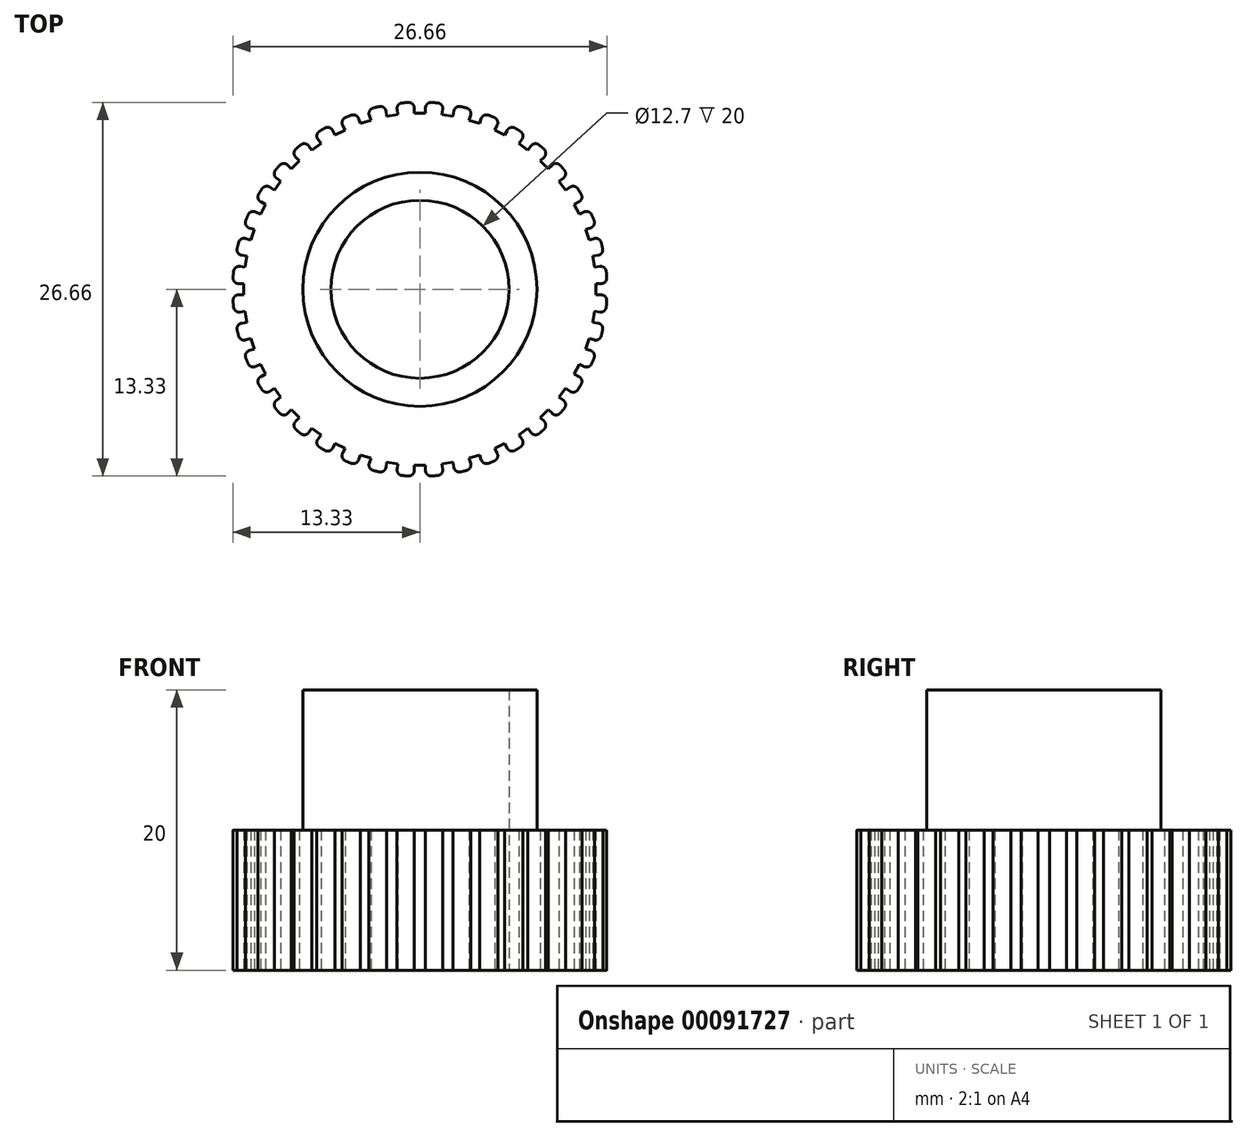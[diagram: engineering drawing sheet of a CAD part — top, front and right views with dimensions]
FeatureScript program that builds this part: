
annotation { "Feature Type Name" : "Feature", "Feature Type Description" : "" }
export const myFeature = defineFeature(function(context is Context, id is Id, definition is map)
    precondition{}
    {
        {
            var Q0;
            Q0=qCreatedBy(makeId("Top.planeOp"),FACE);
            var sketch = newSketch(context, id + "F0", { "sketchPlane" : qUnion([Q0])});
            skCircle(sketch, "E0", {"center": v(0, 0) * mm, "radius": 6.35 * mm});
            skCircle(sketch, "E1", {"center": v(0, 0) * mm, "radius": 8.35 * mm});
            skCircle(sketch, "E2", {"center": v(0, 0) * mm, "radius": 13.35 * mm});
            skLineSegment(sketch, "E3", {"start": v(0, 0) * mm, "end": v(0, 13.35) * mm, "construction": true});
            skLineSegment(sketch, "E4", {"start": v(-0.4, 12.93) * mm, "end": v(-0.4, 12.55) * mm});
            skLineSegment(sketch, "E5", {"start": v(-0.4, 12.55) * mm, "end": v(0.4, 12.55) * mm});
            skLineSegment(sketch, "E6", {"start": v(0.4, 12.55) * mm, "end": v(0.4, 12.93) * mm});
            skArc(sketch, "E7", {"start": v(-0.4, 12.93) * mm, "mid": v(-0.53, 13.22) * mm, "end": v(-0.82, 13.32) * mm});
            skPoint(sketch, "E7.second.point", {"position": v(-0.82, 13.32) * mm});
            skPoint(sketch, "E7.third.point.positionSnap0", {"position": v(-0.4, 12.93) * mm});
            skArc(sketch, "E8.MirrorCS", {"start": v(0.4, 12.93) * mm, "mid": v(0.53, 13.22) * mm, "end": v(0.82, 13.32) * mm});
            skArc(sketch, "E9.1.0", {"start": v(-2.42, 12.7) * mm, "mid": v(-2.59, 12.97) * mm, "end": v(-2.9, 13.03) * mm});
            skLineSegment(sketch, "E9.1.1", {"start": v(-2.42, 12.7) * mm, "end": v(-2.36, 12.33) * mm});
            skLineSegment(sketch, "E9.1.2", {"start": v(-2.36, 12.33) * mm, "end": v(-1.57, 12.46) * mm});
            skLineSegment(sketch, "E9.1.3", {"start": v(-1.57, 12.46) * mm, "end": v(-1.63, 12.83) * mm});
            skArc(sketch, "E9.1.4", {"start": v(-1.63, 12.83) * mm, "mid": v(-1.55, 13.14) * mm, "end": v(-1.27, 13.29) * mm});
            skArc(sketch, "E9.2.0", {"start": v(-4.37, 12.17) * mm, "mid": v(-4.58, 12.4) * mm, "end": v(-4.9, 12.42) * mm});
            skLineSegment(sketch, "E9.2.1", {"start": v(-4.37, 12.17) * mm, "end": v(-4.26, 11.81) * mm});
            skLineSegment(sketch, "E9.2.2", {"start": v(-4.26, 11.81) * mm, "end": v(-3.5, 12.06) * mm});
            skLineSegment(sketch, "E9.2.3", {"start": v(-3.5, 12.06) * mm, "end": v(-3.61, 12.42) * mm});
            skArc(sketch, "E9.2.4", {"start": v(-3.61, 12.42) * mm, "mid": v(-3.58, 12.73) * mm, "end": v(-3.33, 12.93) * mm});
            skArc(sketch, "E9.3.0", {"start": v(-6.22, 11.33) * mm, "mid": v(-6.47, 11.54) * mm, "end": v(-6.78, 11.5) * mm});
            skLineSegment(sketch, "E9.3.1", {"start": v(-6.22, 11.33) * mm, "end": v(-6.05, 11) * mm});
            skLineSegment(sketch, "E9.3.2", {"start": v(-6.05, 11) * mm, "end": v(-5.34, 11.36) * mm});
            skLineSegment(sketch, "E9.3.3", {"start": v(-5.34, 11.36) * mm, "end": v(-5.51, 11.7) * mm});
            skArc(sketch, "E9.3.4", {"start": v(-5.51, 11.7) * mm, "mid": v(-5.53, 12.01) * mm, "end": v(-5.31, 12.25) * mm});
            skArc(sketch, "E9.4.0", {"start": v(-7.92, 10.22) * mm, "mid": v(-8.2, 10.38) * mm, "end": v(-8.5, 10.3) * mm});
            skLineSegment(sketch, "E9.4.1", {"start": v(-7.92, 10.22) * mm, "end": v(-7.7, 9.92) * mm});
            skLineSegment(sketch, "E9.4.2", {"start": v(-7.7, 9.92) * mm, "end": v(-7.05, 10.39) * mm});
            skLineSegment(sketch, "E9.4.3", {"start": v(-7.05, 10.39) * mm, "end": v(-7.27, 10.7) * mm});
            skArc(sketch, "E9.4.4", {"start": v(-7.27, 10.7) * mm, "mid": v(-7.34, 11) * mm, "end": v(-7.16, 11.26) * mm});
            skArc(sketch, "E9.5.0", {"start": v(-9.42, 8.86) * mm, "mid": v(-9.72, 8.97) * mm, "end": v(-10, 8.84) * mm});
            skLineSegment(sketch, "E9.5.1", {"start": v(-9.42, 8.86) * mm, "end": v(-9.16, 8.6) * mm});
            skLineSegment(sketch, "E9.5.2", {"start": v(-9.16, 8.6) * mm, "end": v(-8.6, 9.16) * mm});
            skLineSegment(sketch, "E9.5.3", {"start": v(-8.6, 9.16) * mm, "end": v(-8.86, 9.42) * mm});
            skArc(sketch, "E9.5.4", {"start": v(-8.86, 9.42) * mm, "mid": v(-8.97, 9.72) * mm, "end": v(-8.84, 10) * mm});
            skArc(sketch, "E9.6.0", {"start": v(-10.7, 7.27) * mm, "mid": v(-11, 7.34) * mm, "end": v(-11.26, 7.16) * mm});
            skLineSegment(sketch, "E9.6.1", {"start": v(-10.7, 7.27) * mm, "end": v(-10.39, 7.05) * mm});
            skLineSegment(sketch, "E9.6.2", {"start": v(-10.39, 7.05) * mm, "end": v(-9.92, 7.7) * mm});
            skLineSegment(sketch, "E9.6.3", {"start": v(-9.92, 7.7) * mm, "end": v(-10.22, 7.92) * mm});
            skArc(sketch, "E9.6.4", {"start": v(-10.22, 7.92) * mm, "mid": v(-10.38, 8.2) * mm, "end": v(-10.3, 8.5) * mm});
            skArc(sketch, "E9.7.0", {"start": v(-11.7, 5.51) * mm, "mid": v(-12.01, 5.53) * mm, "end": v(-12.25, 5.31) * mm});
            skLineSegment(sketch, "E9.7.1", {"start": v(-11.7, 5.51) * mm, "end": v(-11.36, 5.34) * mm});
            skLineSegment(sketch, "E9.7.2", {"start": v(-11.36, 5.34) * mm, "end": v(-11, 6.05) * mm});
            skLineSegment(sketch, "E9.7.3", {"start": v(-11, 6.05) * mm, "end": v(-11.33, 6.22) * mm});
            skArc(sketch, "E9.7.4", {"start": v(-11.33, 6.22) * mm, "mid": v(-11.54, 6.47) * mm, "end": v(-11.5, 6.78) * mm});
            skArc(sketch, "E9.8.0", {"start": v(-12.42, 3.61) * mm, "mid": v(-12.73, 3.58) * mm, "end": v(-12.93, 3.33) * mm});
            skLineSegment(sketch, "E9.8.1", {"start": v(-12.42, 3.61) * mm, "end": v(-12.06, 3.5) * mm});
            skLineSegment(sketch, "E9.8.2", {"start": v(-12.06, 3.5) * mm, "end": v(-11.81, 4.26) * mm});
            skLineSegment(sketch, "E9.8.3", {"start": v(-11.81, 4.26) * mm, "end": v(-12.17, 4.37) * mm});
            skArc(sketch, "E9.8.4", {"start": v(-12.17, 4.37) * mm, "mid": v(-12.4, 4.58) * mm, "end": v(-12.42, 4.9) * mm});
            skArc(sketch, "E9.9.0", {"start": v(-12.83, 1.63) * mm, "mid": v(-13.14, 1.55) * mm, "end": v(-13.29, 1.27) * mm});
            skLineSegment(sketch, "E9.9.1", {"start": v(-12.83, 1.63) * mm, "end": v(-12.46, 1.57) * mm});
            skLineSegment(sketch, "E9.9.2", {"start": v(-12.46, 1.57) * mm, "end": v(-12.33, 2.36) * mm});
            skLineSegment(sketch, "E9.9.3", {"start": v(-12.33, 2.36) * mm, "end": v(-12.7, 2.42) * mm});
            skArc(sketch, "E9.9.4", {"start": v(-12.7, 2.42) * mm, "mid": v(-12.97, 2.59) * mm, "end": v(-13.03, 2.9) * mm});
            skArc(sketch, "E9.10.0", {"start": v(-12.93, -0.4) * mm, "mid": v(-13.22, -0.53) * mm, "end": v(-13.32, -0.82) * mm});
            skLineSegment(sketch, "E9.10.1", {"start": v(-12.93, -0.4) * mm, "end": v(-12.55, -0.4) * mm});
            skLineSegment(sketch, "E9.10.2", {"start": v(-12.55, -0.4) * mm, "end": v(-12.55, 0.4) * mm});
            skLineSegment(sketch, "E9.10.3", {"start": v(-12.55, 0.4) * mm, "end": v(-12.93, 0.4) * mm});
            skArc(sketch, "E9.10.4", {"start": v(-12.93, 0.4) * mm, "mid": v(-13.22, 0.53) * mm, "end": v(-13.32, 0.82) * mm});
            skArc(sketch, "E9.11.0", {"start": v(-12.7, -2.42) * mm, "mid": v(-12.97, -2.59) * mm, "end": v(-13.03, -2.9) * mm});
            skLineSegment(sketch, "E9.11.1", {"start": v(-12.7, -2.42) * mm, "end": v(-12.33, -2.36) * mm});
            skLineSegment(sketch, "E9.11.2", {"start": v(-12.33, -2.36) * mm, "end": v(-12.46, -1.57) * mm});
            skLineSegment(sketch, "E9.11.3", {"start": v(-12.46, -1.57) * mm, "end": v(-12.83, -1.63) * mm});
            skArc(sketch, "E9.11.4", {"start": v(-12.83, -1.63) * mm, "mid": v(-13.14, -1.55) * mm, "end": v(-13.29, -1.27) * mm});
            skArc(sketch, "E9.12.0", {"start": v(-12.17, -4.37) * mm, "mid": v(-12.4, -4.58) * mm, "end": v(-12.42, -4.9) * mm});
            skLineSegment(sketch, "E9.12.1", {"start": v(-12.17, -4.37) * mm, "end": v(-11.81, -4.26) * mm});
            skLineSegment(sketch, "E9.12.2", {"start": v(-11.81, -4.26) * mm, "end": v(-12.06, -3.5) * mm});
            skLineSegment(sketch, "E9.12.3", {"start": v(-12.06, -3.5) * mm, "end": v(-12.42, -3.61) * mm});
            skArc(sketch, "E9.12.4", {"start": v(-12.42, -3.61) * mm, "mid": v(-12.73, -3.58) * mm, "end": v(-12.93, -3.33) * mm});
            skArc(sketch, "E9.13.0", {"start": v(-11.33, -6.22) * mm, "mid": v(-11.54, -6.47) * mm, "end": v(-11.5, -6.78) * mm});
            skLineSegment(sketch, "E9.13.1", {"start": v(-11.33, -6.22) * mm, "end": v(-11, -6.05) * mm});
            skLineSegment(sketch, "E9.13.2", {"start": v(-11, -6.05) * mm, "end": v(-11.36, -5.34) * mm});
            skLineSegment(sketch, "E9.13.3", {"start": v(-11.36, -5.34) * mm, "end": v(-11.7, -5.51) * mm});
            skArc(sketch, "E9.13.4", {"start": v(-11.7, -5.51) * mm, "mid": v(-12.01, -5.53) * mm, "end": v(-12.25, -5.31) * mm});
            skArc(sketch, "E9.14.0", {"start": v(-10.22, -7.92) * mm, "mid": v(-10.38, -8.2) * mm, "end": v(-10.3, -8.5) * mm});
            skLineSegment(sketch, "E9.14.1", {"start": v(-10.22, -7.92) * mm, "end": v(-9.92, -7.7) * mm});
            skLineSegment(sketch, "E9.14.2", {"start": v(-9.92, -7.7) * mm, "end": v(-10.39, -7.05) * mm});
            skLineSegment(sketch, "E9.14.3", {"start": v(-10.39, -7.05) * mm, "end": v(-10.7, -7.27) * mm});
            skArc(sketch, "E9.14.4", {"start": v(-10.7, -7.27) * mm, "mid": v(-11, -7.34) * mm, "end": v(-11.26, -7.16) * mm});
            skArc(sketch, "E9.15.0", {"start": v(-8.86, -9.42) * mm, "mid": v(-8.97, -9.72) * mm, "end": v(-8.84, -10) * mm});
            skLineSegment(sketch, "E9.15.1", {"start": v(-8.86, -9.42) * mm, "end": v(-8.6, -9.16) * mm});
            skLineSegment(sketch, "E9.15.2", {"start": v(-8.6, -9.16) * mm, "end": v(-9.16, -8.6) * mm});
            skLineSegment(sketch, "E9.15.3", {"start": v(-9.16, -8.6) * mm, "end": v(-9.42, -8.86) * mm});
            skArc(sketch, "E9.15.4", {"start": v(-9.42, -8.86) * mm, "mid": v(-9.72, -8.97) * mm, "end": v(-10, -8.84) * mm});
            skArc(sketch, "E9.16.0", {"start": v(-7.27, -10.7) * mm, "mid": v(-7.34, -11) * mm, "end": v(-7.16, -11.26) * mm});
            skLineSegment(sketch, "E9.16.1", {"start": v(-7.27, -10.7) * mm, "end": v(-7.05, -10.39) * mm});
            skLineSegment(sketch, "E9.16.2", {"start": v(-7.05, -10.39) * mm, "end": v(-7.7, -9.92) * mm});
            skLineSegment(sketch, "E9.16.3", {"start": v(-7.7, -9.92) * mm, "end": v(-7.92, -10.22) * mm});
            skArc(sketch, "E9.16.4", {"start": v(-7.92, -10.22) * mm, "mid": v(-8.2, -10.38) * mm, "end": v(-8.5, -10.3) * mm});
            skArc(sketch, "E9.17.0", {"start": v(-5.51, -11.7) * mm, "mid": v(-5.53, -12.01) * mm, "end": v(-5.31, -12.25) * mm});
            skLineSegment(sketch, "E9.17.1", {"start": v(-5.51, -11.7) * mm, "end": v(-5.34, -11.36) * mm});
            skLineSegment(sketch, "E9.17.2", {"start": v(-5.34, -11.36) * mm, "end": v(-6.05, -11) * mm});
            skLineSegment(sketch, "E9.17.3", {"start": v(-6.05, -11) * mm, "end": v(-6.22, -11.33) * mm});
            skArc(sketch, "E9.17.4", {"start": v(-6.22, -11.33) * mm, "mid": v(-6.47, -11.54) * mm, "end": v(-6.78, -11.5) * mm});
            skArc(sketch, "E9.18.0", {"start": v(-3.61, -12.42) * mm, "mid": v(-3.58, -12.73) * mm, "end": v(-3.33, -12.93) * mm});
            skLineSegment(sketch, "E9.18.1", {"start": v(-3.61, -12.42) * mm, "end": v(-3.5, -12.06) * mm});
            skLineSegment(sketch, "E9.18.2", {"start": v(-3.5, -12.06) * mm, "end": v(-4.26, -11.81) * mm});
            skLineSegment(sketch, "E9.18.3", {"start": v(-4.26, -11.81) * mm, "end": v(-4.37, -12.17) * mm});
            skArc(sketch, "E9.18.4", {"start": v(-4.37, -12.17) * mm, "mid": v(-4.58, -12.4) * mm, "end": v(-4.9, -12.42) * mm});
            skArc(sketch, "E9.19.0", {"start": v(-1.63, -12.83) * mm, "mid": v(-1.55, -13.14) * mm, "end": v(-1.27, -13.29) * mm});
            skLineSegment(sketch, "E9.19.1", {"start": v(-1.63, -12.83) * mm, "end": v(-1.57, -12.46) * mm});
            skLineSegment(sketch, "E9.19.2", {"start": v(-1.57, -12.46) * mm, "end": v(-2.36, -12.33) * mm});
            skLineSegment(sketch, "E9.19.3", {"start": v(-2.36, -12.33) * mm, "end": v(-2.42, -12.7) * mm});
            skArc(sketch, "E9.19.4", {"start": v(-2.42, -12.7) * mm, "mid": v(-2.59, -12.97) * mm, "end": v(-2.9, -13.03) * mm});
            skArc(sketch, "E9.20.0", {"start": v(0.4, -12.93) * mm, "mid": v(0.53, -13.22) * mm, "end": v(0.82, -13.32) * mm});
            skLineSegment(sketch, "E9.20.1", {"start": v(0.4, -12.93) * mm, "end": v(0.4, -12.55) * mm});
            skLineSegment(sketch, "E9.20.2", {"start": v(0.4, -12.55) * mm, "end": v(-0.4, -12.55) * mm});
            skLineSegment(sketch, "E9.20.3", {"start": v(-0.4, -12.55) * mm, "end": v(-0.4, -12.93) * mm});
            skArc(sketch, "E9.20.4", {"start": v(-0.4, -12.93) * mm, "mid": v(-0.53, -13.22) * mm, "end": v(-0.82, -13.32) * mm});
            skArc(sketch, "E9.21.0", {"start": v(2.42, -12.7) * mm, "mid": v(2.59, -12.97) * mm, "end": v(2.9, -13.03) * mm});
            skLineSegment(sketch, "E9.21.1", {"start": v(2.42, -12.7) * mm, "end": v(2.36, -12.33) * mm});
            skLineSegment(sketch, "E9.21.2", {"start": v(2.36, -12.33) * mm, "end": v(1.57, -12.46) * mm});
            skLineSegment(sketch, "E9.21.3", {"start": v(1.57, -12.46) * mm, "end": v(1.63, -12.83) * mm});
            skArc(sketch, "E9.21.4", {"start": v(1.63, -12.83) * mm, "mid": v(1.55, -13.14) * mm, "end": v(1.27, -13.29) * mm});
            skArc(sketch, "E9.22.0", {"start": v(4.37, -12.17) * mm, "mid": v(4.58, -12.4) * mm, "end": v(4.9, -12.42) * mm});
            skLineSegment(sketch, "E9.22.1", {"start": v(4.37, -12.17) * mm, "end": v(4.26, -11.81) * mm});
            skLineSegment(sketch, "E9.22.2", {"start": v(4.26, -11.81) * mm, "end": v(3.5, -12.06) * mm});
            skLineSegment(sketch, "E9.22.3", {"start": v(3.5, -12.06) * mm, "end": v(3.61, -12.42) * mm});
            skArc(sketch, "E9.22.4", {"start": v(3.61, -12.42) * mm, "mid": v(3.58, -12.73) * mm, "end": v(3.33, -12.93) * mm});
            skArc(sketch, "E9.23.0", {"start": v(6.22, -11.33) * mm, "mid": v(6.47, -11.54) * mm, "end": v(6.78, -11.5) * mm});
            skLineSegment(sketch, "E9.23.1", {"start": v(6.22, -11.33) * mm, "end": v(6.05, -11) * mm});
            skLineSegment(sketch, "E9.23.2", {"start": v(6.05, -11) * mm, "end": v(5.34, -11.36) * mm});
            skLineSegment(sketch, "E9.23.3", {"start": v(5.34, -11.36) * mm, "end": v(5.51, -11.7) * mm});
            skArc(sketch, "E9.23.4", {"start": v(5.51, -11.7) * mm, "mid": v(5.53, -12.01) * mm, "end": v(5.31, -12.25) * mm});
            skArc(sketch, "E9.24.0", {"start": v(7.92, -10.22) * mm, "mid": v(8.2, -10.38) * mm, "end": v(8.5, -10.3) * mm});
            skLineSegment(sketch, "E9.24.1", {"start": v(7.92, -10.22) * mm, "end": v(7.7, -9.92) * mm});
            skLineSegment(sketch, "E9.24.2", {"start": v(7.7, -9.92) * mm, "end": v(7.05, -10.39) * mm});
            skLineSegment(sketch, "E9.24.3", {"start": v(7.05, -10.39) * mm, "end": v(7.27, -10.7) * mm});
            skArc(sketch, "E9.24.4", {"start": v(7.27, -10.7) * mm, "mid": v(7.34, -11) * mm, "end": v(7.16, -11.26) * mm});
            skArc(sketch, "E9.25.0", {"start": v(9.42, -8.86) * mm, "mid": v(9.72, -8.97) * mm, "end": v(10, -8.84) * mm});
            skLineSegment(sketch, "E9.25.1", {"start": v(9.42, -8.86) * mm, "end": v(9.16, -8.6) * mm});
            skLineSegment(sketch, "E9.25.2", {"start": v(9.16, -8.6) * mm, "end": v(8.6, -9.16) * mm});
            skLineSegment(sketch, "E9.25.3", {"start": v(8.6, -9.16) * mm, "end": v(8.86, -9.42) * mm});
            skArc(sketch, "E9.25.4", {"start": v(8.86, -9.42) * mm, "mid": v(8.97, -9.72) * mm, "end": v(8.84, -10) * mm});
            skArc(sketch, "E9.26.0", {"start": v(10.7, -7.27) * mm, "mid": v(11, -7.34) * mm, "end": v(11.26, -7.16) * mm});
            skLineSegment(sketch, "E9.26.1", {"start": v(10.7, -7.27) * mm, "end": v(10.39, -7.05) * mm});
            skLineSegment(sketch, "E9.26.2", {"start": v(10.39, -7.05) * mm, "end": v(9.92, -7.7) * mm});
            skLineSegment(sketch, "E9.26.3", {"start": v(9.92, -7.7) * mm, "end": v(10.22, -7.92) * mm});
            skArc(sketch, "E9.26.4", {"start": v(10.22, -7.92) * mm, "mid": v(10.38, -8.2) * mm, "end": v(10.3, -8.5) * mm});
            skArc(sketch, "E9.27.0", {"start": v(11.7, -5.51) * mm, "mid": v(12.01, -5.53) * mm, "end": v(12.25, -5.31) * mm});
            skLineSegment(sketch, "E9.27.1", {"start": v(11.7, -5.51) * mm, "end": v(11.36, -5.34) * mm});
            skLineSegment(sketch, "E9.27.2", {"start": v(11.36, -5.34) * mm, "end": v(11, -6.05) * mm});
            skLineSegment(sketch, "E9.27.3", {"start": v(11, -6.05) * mm, "end": v(11.33, -6.22) * mm});
            skArc(sketch, "E9.27.4", {"start": v(11.33, -6.22) * mm, "mid": v(11.54, -6.47) * mm, "end": v(11.5, -6.78) * mm});
            skArc(sketch, "E9.28.0", {"start": v(12.42, -3.61) * mm, "mid": v(12.73, -3.58) * mm, "end": v(12.93, -3.33) * mm});
            skLineSegment(sketch, "E9.28.1", {"start": v(12.42, -3.61) * mm, "end": v(12.06, -3.5) * mm});
            skLineSegment(sketch, "E9.28.2", {"start": v(12.06, -3.5) * mm, "end": v(11.81, -4.26) * mm});
            skLineSegment(sketch, "E9.28.3", {"start": v(11.81, -4.26) * mm, "end": v(12.17, -4.37) * mm});
            skArc(sketch, "E9.28.4", {"start": v(12.17, -4.37) * mm, "mid": v(12.4, -4.58) * mm, "end": v(12.42, -4.9) * mm});
            skArc(sketch, "E9.29.0", {"start": v(12.83, -1.63) * mm, "mid": v(13.14, -1.55) * mm, "end": v(13.29, -1.27) * mm});
            skLineSegment(sketch, "E9.29.1", {"start": v(12.83, -1.63) * mm, "end": v(12.46, -1.57) * mm});
            skLineSegment(sketch, "E9.29.2", {"start": v(12.46, -1.57) * mm, "end": v(12.33, -2.36) * mm});
            skLineSegment(sketch, "E9.29.3", {"start": v(12.33, -2.36) * mm, "end": v(12.7, -2.42) * mm});
            skArc(sketch, "E9.29.4", {"start": v(12.7, -2.42) * mm, "mid": v(12.97, -2.59) * mm, "end": v(13.03, -2.9) * mm});
            skArc(sketch, "E9.30.0", {"start": v(12.93, 0.4) * mm, "mid": v(13.22, 0.53) * mm, "end": v(13.32, 0.82) * mm});
            skLineSegment(sketch, "E9.30.1", {"start": v(12.93, 0.4) * mm, "end": v(12.55, 0.4) * mm});
            skLineSegment(sketch, "E9.30.2", {"start": v(12.55, 0.4) * mm, "end": v(12.55, -0.4) * mm});
            skLineSegment(sketch, "E9.30.3", {"start": v(12.55, -0.4) * mm, "end": v(12.93, -0.4) * mm});
            skArc(sketch, "E9.30.4", {"start": v(12.93, -0.4) * mm, "mid": v(13.22, -0.53) * mm, "end": v(13.32, -0.82) * mm});
            skArc(sketch, "E9.31.0", {"start": v(12.7, 2.42) * mm, "mid": v(12.97, 2.59) * mm, "end": v(13.03, 2.9) * mm});
            skLineSegment(sketch, "E9.31.1", {"start": v(12.7, 2.42) * mm, "end": v(12.33, 2.36) * mm});
            skLineSegment(sketch, "E9.31.2", {"start": v(12.33, 2.36) * mm, "end": v(12.46, 1.57) * mm});
            skLineSegment(sketch, "E9.31.3", {"start": v(12.46, 1.57) * mm, "end": v(12.83, 1.63) * mm});
            skArc(sketch, "E9.31.4", {"start": v(12.83, 1.63) * mm, "mid": v(13.14, 1.55) * mm, "end": v(13.29, 1.27) * mm});
            skArc(sketch, "E9.32.0", {"start": v(12.17, 4.37) * mm, "mid": v(12.4, 4.58) * mm, "end": v(12.42, 4.9) * mm});
            skLineSegment(sketch, "E9.32.1", {"start": v(12.17, 4.37) * mm, "end": v(11.81, 4.26) * mm});
            skLineSegment(sketch, "E9.32.2", {"start": v(11.81, 4.26) * mm, "end": v(12.06, 3.5) * mm});
            skLineSegment(sketch, "E9.32.3", {"start": v(12.06, 3.5) * mm, "end": v(12.42, 3.61) * mm});
            skArc(sketch, "E9.32.4", {"start": v(12.42, 3.61) * mm, "mid": v(12.73, 3.58) * mm, "end": v(12.93, 3.33) * mm});
            skArc(sketch, "E9.33.0", {"start": v(11.33, 6.22) * mm, "mid": v(11.54, 6.47) * mm, "end": v(11.5, 6.78) * mm});
            skLineSegment(sketch, "E9.33.1", {"start": v(11.33, 6.22) * mm, "end": v(11, 6.05) * mm});
            skLineSegment(sketch, "E9.33.2", {"start": v(11, 6.05) * mm, "end": v(11.36, 5.34) * mm});
            skLineSegment(sketch, "E9.33.3", {"start": v(11.36, 5.34) * mm, "end": v(11.7, 5.51) * mm});
            skArc(sketch, "E9.33.4", {"start": v(11.7, 5.51) * mm, "mid": v(12.01, 5.53) * mm, "end": v(12.25, 5.31) * mm});
            skArc(sketch, "E9.34.0", {"start": v(10.22, 7.92) * mm, "mid": v(10.38, 8.2) * mm, "end": v(10.3, 8.5) * mm});
            skLineSegment(sketch, "E9.34.1", {"start": v(10.22, 7.92) * mm, "end": v(9.92, 7.7) * mm});
            skLineSegment(sketch, "E9.34.2", {"start": v(9.92, 7.7) * mm, "end": v(10.39, 7.05) * mm});
            skLineSegment(sketch, "E9.34.3", {"start": v(10.39, 7.05) * mm, "end": v(10.7, 7.27) * mm});
            skArc(sketch, "E9.34.4", {"start": v(10.7, 7.27) * mm, "mid": v(11, 7.34) * mm, "end": v(11.26, 7.16) * mm});
            skArc(sketch, "E9.35.0", {"start": v(8.86, 9.42) * mm, "mid": v(8.97, 9.72) * mm, "end": v(8.84, 10) * mm});
            skLineSegment(sketch, "E9.35.1", {"start": v(8.86, 9.42) * mm, "end": v(8.6, 9.16) * mm});
            skLineSegment(sketch, "E9.35.2", {"start": v(8.6, 9.16) * mm, "end": v(9.16, 8.6) * mm});
            skLineSegment(sketch, "E9.35.3", {"start": v(9.16, 8.6) * mm, "end": v(9.42, 8.86) * mm});
            skArc(sketch, "E9.35.4", {"start": v(9.42, 8.86) * mm, "mid": v(9.72, 8.97) * mm, "end": v(10, 8.84) * mm});
            skArc(sketch, "E9.36.0", {"start": v(7.27, 10.7) * mm, "mid": v(7.34, 11) * mm, "end": v(7.16, 11.26) * mm});
            skLineSegment(sketch, "E9.36.1", {"start": v(7.27, 10.7) * mm, "end": v(7.05, 10.39) * mm});
            skLineSegment(sketch, "E9.36.2", {"start": v(7.05, 10.39) * mm, "end": v(7.7, 9.92) * mm});
            skLineSegment(sketch, "E9.36.3", {"start": v(7.7, 9.92) * mm, "end": v(7.92, 10.22) * mm});
            skArc(sketch, "E9.36.4", {"start": v(7.92, 10.22) * mm, "mid": v(8.2, 10.38) * mm, "end": v(8.5, 10.3) * mm});
            skArc(sketch, "E9.37.0", {"start": v(5.51, 11.7) * mm, "mid": v(5.53, 12.01) * mm, "end": v(5.31, 12.25) * mm});
            skLineSegment(sketch, "E9.37.1", {"start": v(5.51, 11.7) * mm, "end": v(5.34, 11.36) * mm});
            skLineSegment(sketch, "E9.37.2", {"start": v(5.34, 11.36) * mm, "end": v(6.05, 11) * mm});
            skLineSegment(sketch, "E9.37.3", {"start": v(6.05, 11) * mm, "end": v(6.22, 11.33) * mm});
            skArc(sketch, "E9.37.4", {"start": v(6.22, 11.33) * mm, "mid": v(6.47, 11.54) * mm, "end": v(6.78, 11.5) * mm});
            skArc(sketch, "E9.38.0", {"start": v(3.61, 12.42) * mm, "mid": v(3.58, 12.73) * mm, "end": v(3.33, 12.93) * mm});
            skLineSegment(sketch, "E9.38.1", {"start": v(3.61, 12.42) * mm, "end": v(3.5, 12.06) * mm});
            skLineSegment(sketch, "E9.38.2", {"start": v(3.5, 12.06) * mm, "end": v(4.26, 11.81) * mm});
            skLineSegment(sketch, "E9.38.3", {"start": v(4.26, 11.81) * mm, "end": v(4.37, 12.17) * mm});
            skArc(sketch, "E9.38.4", {"start": v(4.37, 12.17) * mm, "mid": v(4.58, 12.4) * mm, "end": v(4.9, 12.42) * mm});
            skArc(sketch, "E9.39.0", {"start": v(1.63, 12.83) * mm, "mid": v(1.55, 13.14) * mm, "end": v(1.27, 13.29) * mm});
            skLineSegment(sketch, "E9.39.1", {"start": v(1.63, 12.83) * mm, "end": v(1.57, 12.46) * mm});
            skLineSegment(sketch, "E9.39.2", {"start": v(1.57, 12.46) * mm, "end": v(2.36, 12.33) * mm});
            skLineSegment(sketch, "E9.39.3", {"start": v(2.36, 12.33) * mm, "end": v(2.42, 12.7) * mm});
            skArc(sketch, "E9.39.4", {"start": v(2.42, 12.7) * mm, "mid": v(2.59, 12.97) * mm, "end": v(2.9, 13.03) * mm});
            skSolve(sketch);
        }
        {
            var Q0;
            Q0=makeQuery(id+"F0.imprint","IMPRINT",FACE,{"disambiguationData":[TD([[makeQuery(id+"F0.imprint","IMPRINT",EDGE,{"derivedFrom":sQuery(id+"F0.wireOp",EDGE,"E0")}),-1.0]])]});
            extrude(context, id + "F1", {"entities" : qUnion([Q0]), "depth" : 20 * mm});
        }
        {
            var Q0;
            Q0=makeQuery(id+"F0.imprint","IMPRINT",FACE,{"disambiguationData":[TD([[makeQuery(id+"F0.imprint","IMPRINT",EDGE,{"derivedFrom":sQuery(id+"F0.wireOp",EDGE,"E1")}),-1.0]])]});
            extrude(context, id + "F2", {"entities" : qUnion([Q0]), "operationType" : NewBodyOperationType.ADD, "depth" : 10 * mm});
        }
    });
